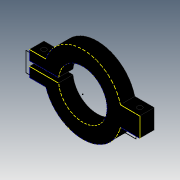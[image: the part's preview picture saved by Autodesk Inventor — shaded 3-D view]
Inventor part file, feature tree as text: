
AUTODESK INVENTOR PART (.ipt)
format: ipt  version: 2015 (Build 190159000, 159)  size: 139,776 bytes
history: native  units: mm
features: other x5, sketch x4, extrude x3, projected_geometry x1
ambient origin geometry x8: Origin, YZ Plane, XZ Plane, XY Plane, X Axis, Y Axis, Z Axis, Center Point
bodies: Solid1 (feature_tree)
feature tree (13):
  other  "Blocks"
  extrude  "Extrusion1"  Depth=160.0mm
  extrude  "Extrusion2"  Depth=20.0mm
  extrude  "Extrusion3"  Depth=10.0mm
  sketch  "Sketch5"  dims[d9=15.0mm d10=15.0mm d11=30.0mm d12=0.0mm d13=20.0mm d14=40.0mm d15=10.0mm d16=15.0mm d17=15.0mm d18=30.0mm d19=0.0mm d20=60.0mm]
  other  "DXF"
  sketch  "Sketch1"  dims[d0=100.0mm d1=160.0mm]
  sketch  "Sketch3"  dims[d4=5.0mm d5=20.0mm]
  sketch  "Sketch4"  dims[d6=30.0mm d7=0.0mm d8=10.0mm]
  projected_geometry  "Projected Loop1"
  other  "Block1"
  other  "Block1:1"
  other  "Block1:2"
